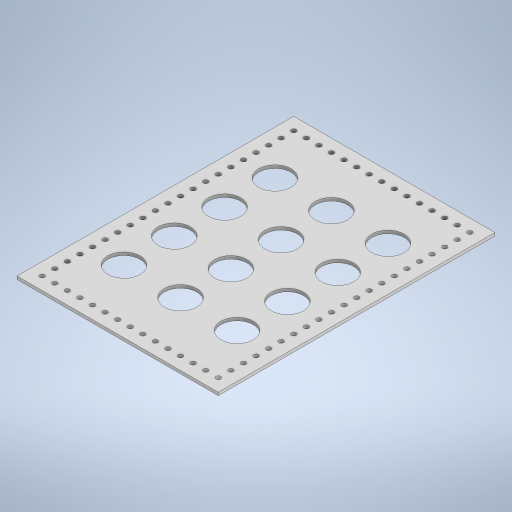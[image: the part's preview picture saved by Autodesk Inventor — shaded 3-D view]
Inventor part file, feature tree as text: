
AUTODESK INVENTOR PART (.ipt)
format: ipt  version: 2023.4 (Build 274418000, 418)  size: 403,456 bytes
history: native  units: in
note: dims shown in document units (in); Inventor stores cm internally (conversion verified against a paired STEP export)
features: sketch x3, extrude x2, sheet_metal_op x1, other x1
ambient origin geometry x8: Origin, YZ Plane, XZ Plane, XY Plane, X Axis, Y Axis, Z Axis, Center Point
bodies: Solid1 (feature_tree)
feature tree (7):
  sheet_metal_op  "Face1"
  extrude  "Extrusion1"  Depth=11.0in
  extrude  "Extrusion2"  Depth=0.12in
  sketch  "Sketch1"  dims[d0=8.0in d1=11.0in]
  other  "Plate1"
  sketch  "Sketch2"  dims[d2=0.12in d3=0.197in]
  sketch  "Sketch3"  dims[d4=0.5in d5=0.5in d6=5.5118in d8=0.5in d9=0.3937in d11=1.0in d13=0.197in d15=0.5in d16=0.5in d17=7.874in d19=0.5in d20=0.3937in d22=1.0in d24=0.197in d25=0.5in d26=0.5in d27=5.5118in d29=0.5in d30=0.3937in d32=1.0in d34=0.197in d35=0.5in d36=0.5in d37=7.874in d39=0.5in d40=0.3937in d42=1.0in d44=1.0in d45=0.0in d48=1.0in d49=1.0in d50=1.0in d51=1.0in d52=1.289in d53=1.5748in d55=2.0in d56=0.3937in d58=1.0in d60=5.0in d62=5.0in d63=1.289in d64=2.25in d65=3.5in d66=5.0in d67=1.5748in d69=2.0in d70=0.3937in d72=1.0in d74=1.289in d75=2.25in d76=5.0in d77=1.5748in d79=2.0in d80=0.3937in d82=1.0in d84=1.0in d85=0.0in]
